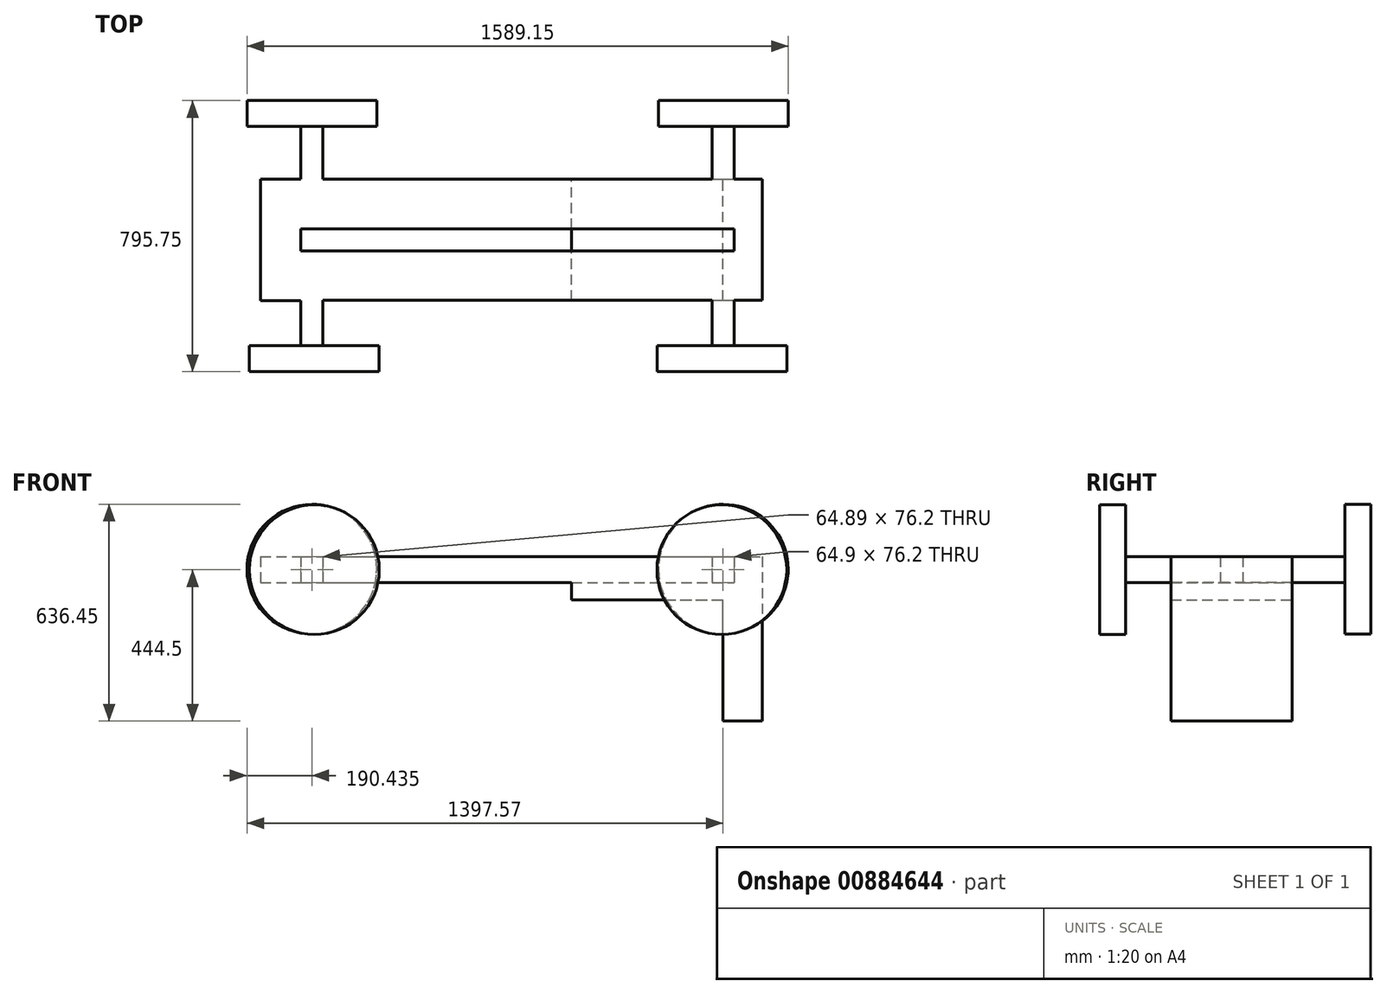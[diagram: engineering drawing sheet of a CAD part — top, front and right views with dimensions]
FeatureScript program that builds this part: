
annotation { "Feature Type Name" : "Feature", "Feature Type Description" : "" }
export const myFeature = defineFeature(function(context is Context, id is Id, definition is map)
    precondition{}
    {
        {
            var Q0;
            Q0=qCreatedBy(makeId("Top.planeOp"),FACE);
            var sketch = newSketch(context, id + "F0", { "sketchPlane" : qUnion([Q0])});
            skLineSegment(sketch, "E0.bottom", {"start": v(112.53, -27.8) * mm, "end": v(1403, -27.8) * mm});
            skLineSegment(sketch, "E0.top", {"start": v(-70.2, 327.8) * mm, "end": v(1403, 327.8) * mm});
            skLineSegment(sketch, "E0.right", {"start": v(1403, -27.8) * mm, "end": v(1403, 327.8) * mm});
            skLineSegment(sketch, "E1.bottom", {"start": v(47.64, -160.7) * mm, "end": v(112.53, -160.7) * mm});
            skLineSegment(sketch, "E1.top", {"start": v(47.64, 482.66) * mm, "end": v(112.53, 482.66) * mm});
            skLineSegment(sketch, "E1.left", {"start": v(47.64, -160.7) * mm, "end": v(47.64, 482.66) * mm});
            skLineSegment(sketch, "E1.right", {"start": v(112.53, -160.7) * mm, "end": v(112.53, 482.66) * mm});
            skLineSegment(sketch, "E2.bottom", {"start": v(539.4, -27.8) * mm, "end": v(539.4, -27.8) * mm});
            skLineSegment(sketch, "E2.top", {"start": v(539.4, 327.8) * mm, "end": v(666.4, 327.8) * mm});
            skLineSegment(sketch, "E3.left", {"start": v(632, -27.8) * mm, "end": v(632, 327.8) * mm});
            skLineSegment(sketch, "E3.right", {"start": v(710.85, -27.8) * mm, "end": v(710.85, 327.8) * mm});
            skPoint(sketch, "E4.orphan", {"position": v(632, -160.7) * mm});
            skPoint(sketch, "E5.orphan", {"position": v(710.85, 482.66) * mm});
            skLineSegment(sketch, "E6.bottom", {"start": v(1254.77, -160.7) * mm, "end": v(1319.67, -160.7) * mm});
            skLineSegment(sketch, "E6.top", {"start": v(1254.77, 482.66) * mm, "end": v(1319.67, 482.66) * mm});
            skLineSegment(sketch, "E6.left", {"start": v(1254.77, -160.7) * mm, "end": v(1254.77, 482.66) * mm});
            skLineSegment(sketch, "E6.right", {"start": v(1319.67, -160.7) * mm, "end": v(1319.67, 482.66) * mm});
            skLineSegment(sketch, "E7.bottom", {"start": v(-70.2, 117.55) * mm, "end": v(1403, 117.55) * mm});
            skLineSegment(sketch, "E7.top", {"start": v(-70.2, 182.44) * mm, "end": v(1403, 182.44) * mm});
            skLineSegment(sketch, "E7.left", {"start": v(-70.2, 117.55) * mm, "end": v(-70.2, 182.44) * mm});
            skPoint(sketch, "E7.middle", {"position": v(710.85, 150) * mm});
            skLineSegment(sketch, "E8", {"start": v(-70.2, 327.8) * mm, "end": v(-70.2, -28.36) * mm});
            skLineSegment(sketch, "E9", {"start": v(-70.2, -28.36) * mm, "end": v(47.64, -28.36) * mm});
            skPoint(sketch, "E7.right.end.orphan", {"position": v(1491.9, 182.44) * mm});
            skPoint(sketch, "E7.right.start.orphan", {"position": v(1491.9, 117.55) * mm});
            skSolve(sketch);
        }
        {
            var Q0;
            Q0 = qSketchRegion(id + "F0", true);
            extrude(context, id + "F1", {"entities" : qUnion([Q0]), "depth" : 76.2 * mm, "offsetDistance" : 25.4 * mm});
        }
        {
            var Q0;
            Q0=makeQuery(id+"F1.opExtrude","SWEPT_FACE",FACE,{"disambiguationData":[OSD([sQuery(id+"F0.wireOp",EDGE,"E1.top")])]});
            var sketch = newSketch(context, id + "F2", { "sketchPlane" : qUnion([Q0])});
            skCircle(sketch, "E10", {"center": v(-80.15, 39.55) * mm, "radius": 190.5 * mm});
            skCircle(sketch, "E11", {"center": v(-1288.3, 39.55) * mm, "radius": 190.5 * mm});
            skSolve(sketch);
        }
        {
            var Q0;
            Q0 = qSketchRegion(id + "F2", true);
            extrude(context, id + "F3", {"entities" : qUnion([Q0]), "operationType" : NewBodyOperationType.ADD, "depth" : 76.2 * mm, "offsetDistance" : 25.4 * mm});
        }
        {
            var Q0;
            Q0=makeQuery(id+"F1.opExtrude","SWEPT_FACE",FACE,{"disambiguationData":[OSD([sQuery(id+"F0.wireOp",EDGE,"E6.bottom")])]});
            var sketch = newSketch(context, id + "F4", { "sketchPlane" : qUnion([Q0])});
            skCircle(sketch, "E12", {"center": v(1283.8, 38.1) * mm, "radius": 190.5 * mm});
            skPoint(sketch, "E12.centerSnap0", {"position": v(1254.77, 38.1) * mm});
            skCircle(sketch, "E13", {"center": v(87.33, 38.1) * mm, "radius": 190.5 * mm});
            skSolve(sketch);
        }
        {
            var Q0;
            Q0 = qSketchRegion(id + "F4", true);
            extrude(context, id + "F5", {"entities" : qUnion([Q0]), "operationType" : NewBodyOperationType.ADD, "depth" : 76.2 * mm, "offsetDistance" : 25.4 * mm});
        }
        {
            var Q0;
            Q0=makeQuery(id+"F1.opExtrude","CAP_FACE",FACE,{"disambiguationData":[OSD([sQuery(id+"F0.wireOp",EDGE,"E0.bottom"),sQuery(id+"F0.wireOp",EDGE,"E0.top"),sQuery(id+"F0.wireOp",EDGE,"E0.right"),sQuery(id+"F0.wireOp",EDGE,"E1.bottom"),sQuery(id+"F0.wireOp",EDGE,"E1.top"),sQuery(id+"F0.wireOp",EDGE,"E1.left"),sQuery(id+"F0.wireOp",EDGE,"E1.right"),sQuery(id+"F0.wireOp",EDGE,"E2.top"),sQuery(id+"F0.wireOp",EDGE,"E6.bottom"),sQuery(id+"F0.wireOp",EDGE,"E6.top"),sQuery(id+"F0.wireOp",EDGE,"E6.left"),sQuery(id+"F0.wireOp",EDGE,"E6.right"),sQuery(id+"F0.wireOp",EDGE,"E7.bottom"),sQuery(id+"F0.wireOp",EDGE,"E7.top"),sQuery(id+"F0.wireOp",EDGE,"E7.right"),sQuery(id+"F0.wireOp",EDGE,"E8"),sQuery(id+"F0.wireOp",EDGE,"E9")])],"isStart":true});
            var sketch = newSketch(context, id + "F6", { "sketchPlane" : qUnion([Q0])});
            skLineSegment(sketch, "E14.bottom", {"start": v(1403, 27.8) * mm, "end": v(842.9, 27.8) * mm});
            skLineSegment(sketch, "E14.top", {"start": v(1403, -327.8) * mm, "end": v(842.9, -327.8) * mm});
            skLineSegment(sketch, "E14.left", {"start": v(1403, 27.8) * mm, "end": v(1403, -327.8) * mm});
            skLineSegment(sketch, "E14.right", {"start": v(842.9, 27.8) * mm, "end": v(842.9, -327.8) * mm});
            skSolve(sketch);
        }
        {
            var Q0;
            Q0 = qSketchRegion(id + "F6", true);
            extrude(context, id + "F7", {"entities" : qUnion([Q0]), "operationType" : NewBodyOperationType.ADD, "depth" : 50.8 * mm, "offsetDistance" : 25.4 * mm});
        }
        {
            var Q0;
            Q0=makeQuery(id+"F7.opExtrude","CAP_FACE",FACE,{"disambiguationData":[OSD([sQuery(id+"F6.wireOp",EDGE,"E14.bottom"),sQuery(id+"F6.wireOp",EDGE,"E14.top"),sQuery(id+"F6.wireOp",EDGE,"E14.left"),sQuery(id+"F6.wireOp",EDGE,"E14.right")])],"isStart":false});
            var sketch = newSketch(context, id + "F8", { "sketchPlane" : qUnion([Q0])});
            skLineSegment(sketch, "E15.bottom", {"start": v(1403, 27.8) * mm, "end": v(1287.06, 27.8) * mm});
            skLineSegment(sketch, "E15.top", {"start": v(1403, -327.8) * mm, "end": v(1287.06, -327.8) * mm});
            skLineSegment(sketch, "E15.left", {"start": v(1403, 27.8) * mm, "end": v(1403, -327.8) * mm});
            skLineSegment(sketch, "E15.right", {"start": v(1287.06, 27.8) * mm, "end": v(1287.06, -327.8) * mm});
            skSolve(sketch);
        }
        {
            var Q0;
            Q0 = qSketchRegion(id + "F8", true);
            extrude(context, id + "F9", {"entities" : qUnion([Q0]), "operationType" : NewBodyOperationType.ADD, "depth" : 355.6 * mm, "offsetDistance" : 25.4 * mm});
        }
    });
